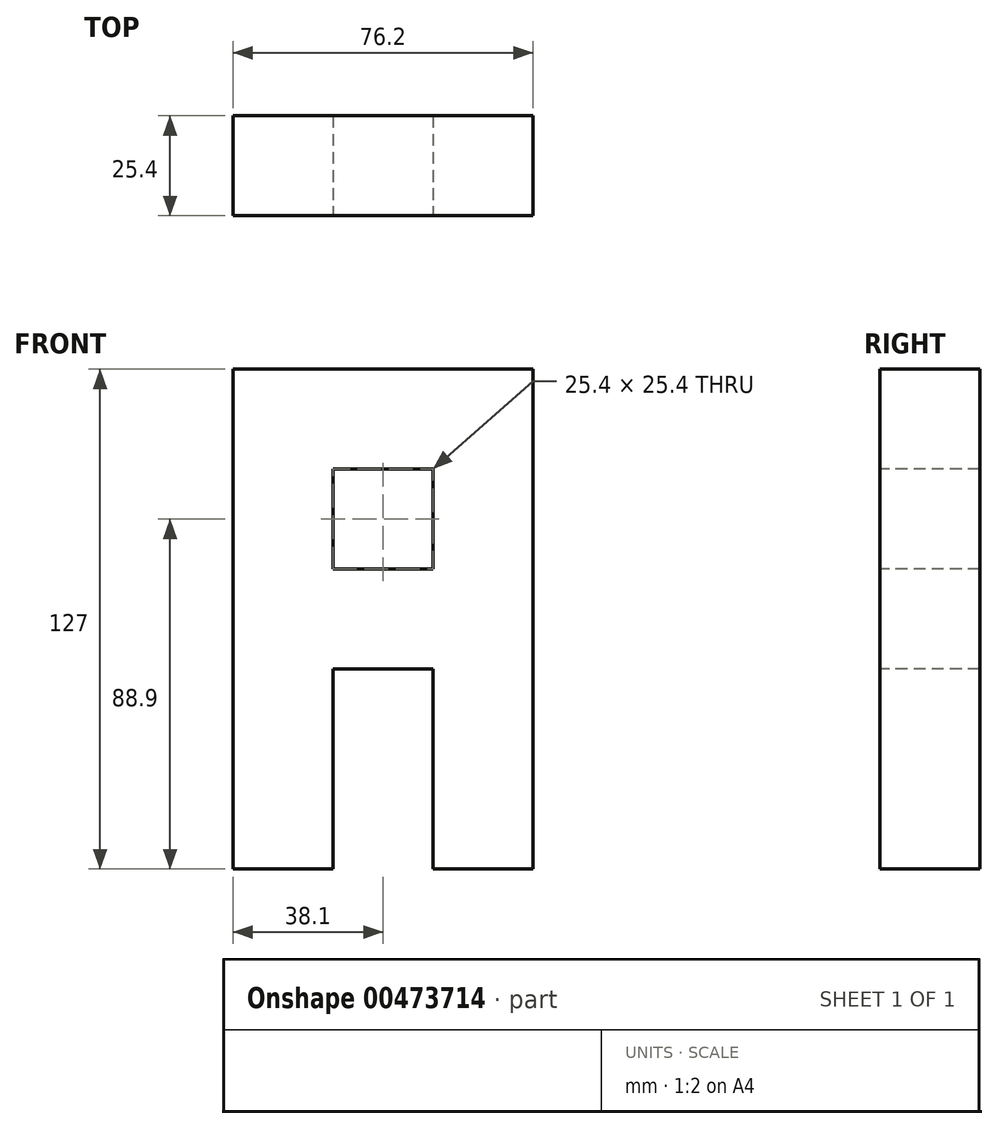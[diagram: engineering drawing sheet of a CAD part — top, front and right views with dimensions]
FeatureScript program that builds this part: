
annotation { "Feature Type Name" : "Feature", "Feature Type Description" : "" }
export const myFeature = defineFeature(function(context is Context, id is Id, definition is map)
    precondition{}
    {
        {
            var Q0;
            Q0=qCreatedBy(makeId("Front.planeOp"),FACE);
            var sketch = newSketch(context, id + "F0", { "sketchPlane" : qUnion([Q0])});
            skLineSegment(sketch, "E0.bottom", {"start": v(38.1, 63.5) * mm, "end": v(-38.1, 63.5) * mm});
            skLineSegment(sketch, "E0.top", {"start": v(38.1, -63.5) * mm, "end": v(-38.1, -63.5) * mm});
            skLineSegment(sketch, "E0.left", {"start": v(38.1, 63.5) * mm, "end": v(38.1, -63.5) * mm});
            skLineSegment(sketch, "E0.right", {"start": v(-38.1, 63.5) * mm, "end": v(-38.1, -63.5) * mm});
            skPoint(sketch, "E0.middle", {"position": v(0, 0) * mm});
            skSolve(sketch);
        }
        {
            var Q0;
            Q0=makeQuery(id+"F0.imprint","IMPRINT",FACE,{"disambiguationData":[TD([[makeQuery(id+"F0.imprint","IMPRINT",EDGE,{"derivedFrom":sQuery(id+"F0.wireOp",EDGE,"E0.bottom")}),1.0]])]});
            extrude(context, id + "F1", {"entities" : qUnion([Q0]), "depth" : 25.4 * mm});
        }
        {
            var Q0;
            Q0=makeQuery(id+"F1.opExtrude","CAP_FACE",FACE,{"disambiguationData":[OSD([sQuery(id+"F0.wireOp",EDGE,"E0.bottom"),sQuery(id+"F0.wireOp",EDGE,"E0.top"),sQuery(id+"F0.wireOp",EDGE,"E0.left"),sQuery(id+"F0.wireOp",EDGE,"E0.right")])],"isStart":false});
            var sketch = newSketch(context, id + "F2", { "sketchPlane" : qUnion([Q0])});
            skLineSegment(sketch, "E1.bottom", {"start": v(-12.7, -63.5) * mm, "end": v(12.7, -63.5) * mm});
            skLineSegment(sketch, "E1.top", {"start": v(-12.7, -12.7) * mm, "end": v(12.7, -12.7) * mm});
            skLineSegment(sketch, "E1.left", {"start": v(-12.7, -63.5) * mm, "end": v(-12.7, -12.7) * mm});
            skLineSegment(sketch, "E1.right", {"start": v(12.7, -63.5) * mm, "end": v(12.7, -12.7) * mm});
            skSolve(sketch);
        }
        {
            var Q0;
            Q0=makeQuery(id+"F2.imprint","IMPRINT",FACE,{"disambiguationData":[TD([[makeQuery(id+"F2.imprint","IMPRINT",EDGE,{"derivedFrom":sQuery(id+"F2.wireOp",EDGE,"E1.bottom")}),-1.0]])]});
            extrude(context, id + "F3", {"entities" : qUnion([Q0]), "operationType" : NewBodyOperationType.REMOVE, "endBound" : BoundingType.THROUGH_ALL, "oppositeDirection" : true, "depth" : 25.4 * mm});
        }
        {
            var Q0;
            Q0=makeQuery(id+"F1.opExtrude","CAP_FACE",FACE,{"disambiguationData":[OSD([sQuery(id+"F0.wireOp",EDGE,"E0.bottom"),sQuery(id+"F0.wireOp",EDGE,"E0.top"),sQuery(id+"F0.wireOp",EDGE,"E0.left"),sQuery(id+"F0.wireOp",EDGE,"E0.right")])],"isStart":false});
            var sketch = newSketch(context, id + "F4", { "sketchPlane" : qUnion([Q0])});
            skLineSegment(sketch, "E2.bottom", {"start": v(-12.7, 38.1) * mm, "end": v(12.7, 38.1) * mm});
            skLineSegment(sketch, "E2.top", {"start": v(-12.7, 12.7) * mm, "end": v(12.7, 12.7) * mm});
            skLineSegment(sketch, "E2.left", {"start": v(-12.7, 38.1) * mm, "end": v(-12.7, 12.7) * mm});
            skLineSegment(sketch, "E2.right", {"start": v(12.7, 38.1) * mm, "end": v(12.7, 12.7) * mm});
            skSolve(sketch);
        }
        {
            var Q0;
            Q0=makeQuery(id+"F4.imprint","IMPRINT",FACE,{"disambiguationData":[TD([[makeQuery(id+"F4.imprint","IMPRINT",EDGE,{"derivedFrom":sQuery(id+"F4.wireOp",EDGE,"E2.bottom")}),-1.0]])]});
            extrude(context, id + "F5", {"entities" : qUnion([Q0]), "operationType" : NewBodyOperationType.REMOVE, "endBound" : BoundingType.THROUGH_ALL, "oppositeDirection" : true, "depth" : 25.4 * mm});
        }
    });
